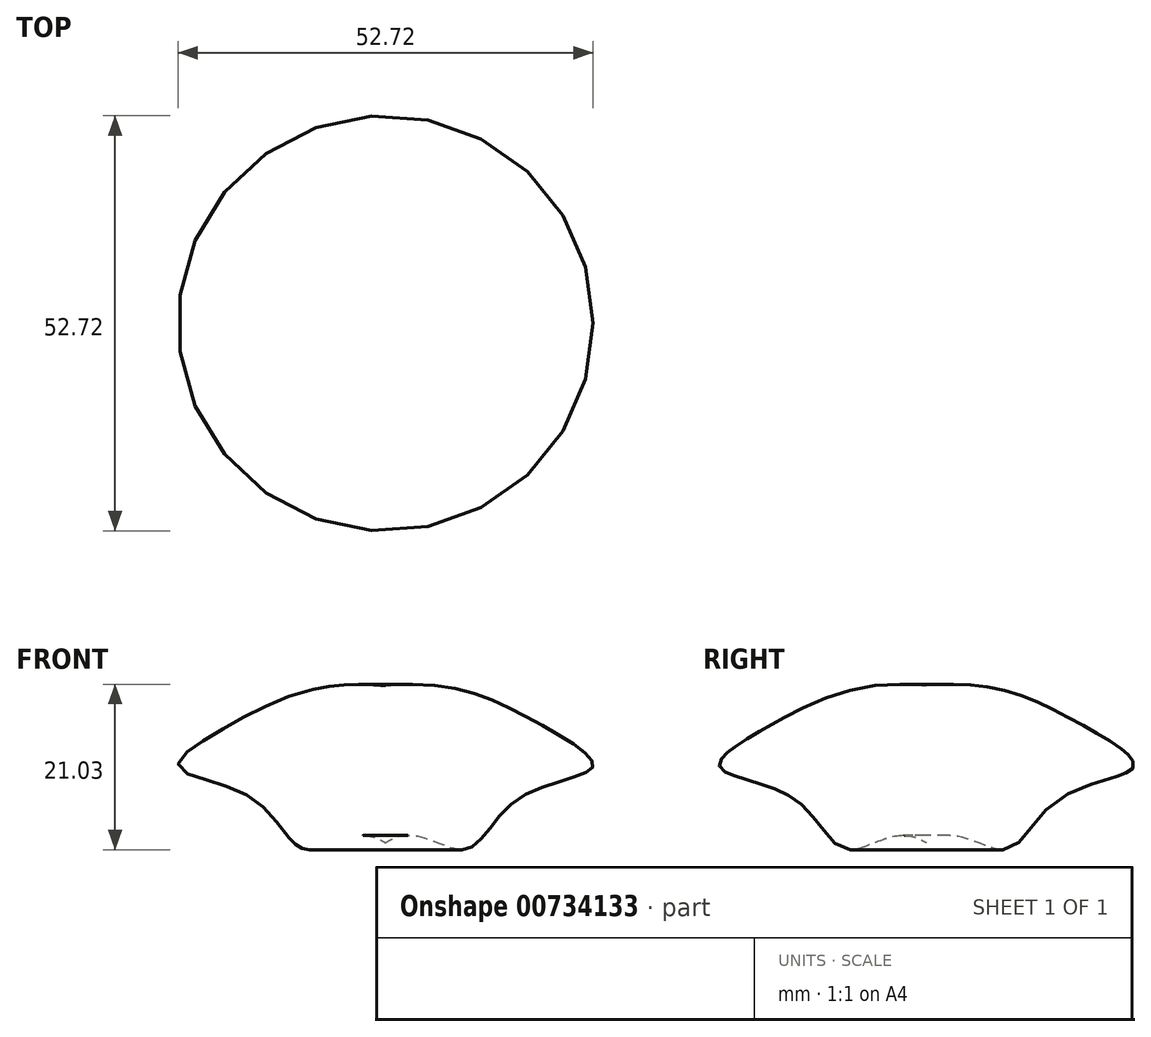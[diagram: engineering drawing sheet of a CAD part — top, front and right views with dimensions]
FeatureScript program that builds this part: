
annotation { "Feature Type Name" : "Feature", "Feature Type Description" : "" }
export const myFeature = defineFeature(function(context is Context, id is Id, definition is map)
    precondition{}
    {
        {
            var Q0;
            Q0=qCreatedBy(makeId("Front.planeOp"),FACE);
            var sketch = newSketch(context, id + "F0", { "sketchPlane" : qUnion([Q0])});
            skLineSegment(sketch, "E0", {"start": v(0, 0) * mm, "end": v(0, 20) * mm});
            skFitSpline(sketch, "E1", {"points": [v(0, 20) * mm, v(19.17, 15.34) * mm, v(26.32, 9.7) * mm, v(16.81, 5.6) * mm, v(9.93, -0.84) * mm, v(0, 0) * mm], "startDerivative": vector(98.9, 10.1) * mm, "endDerivative": vector(-58.05, -42.29) * mm});
            skSolve(sketch);
        }
        {
            var Q0;
            Q0=qCreatedBy(makeId("Front.planeOp"),FACE);
            var sketch = newSketch(context, id + "F1", { "sketchPlane" : qUnion([Q0])});
            skLineSegment(sketch, "E2", {"start": v(0, 61.65) * mm, "end": v(0, -23.97) * mm});
            skSolve(sketch);
        }
        {
            var Q0;
            Q0=makeQuery(id+"F0.imprint","IMPRINT",FACE,{"disambiguationData":[TD([[makeQuery(id+"F0.imprint","IMPRINT",EDGE,{"derivedFrom":sQuery(id+"F0.wireOp",EDGE,"E0")}),-1.0]])]});
            var Q1;
            Q1=sQuery(id+"F1.wireOp",EDGE,"E2");
            revolve(context, id + "F2", {"surfaceOperationType" : NewSurfaceOperationType.NEW, "entities" : qUnion([Q0]), "axis" : qUnion([Q1]), "revolveType" : RevolveType.FULL});
        }
    });
